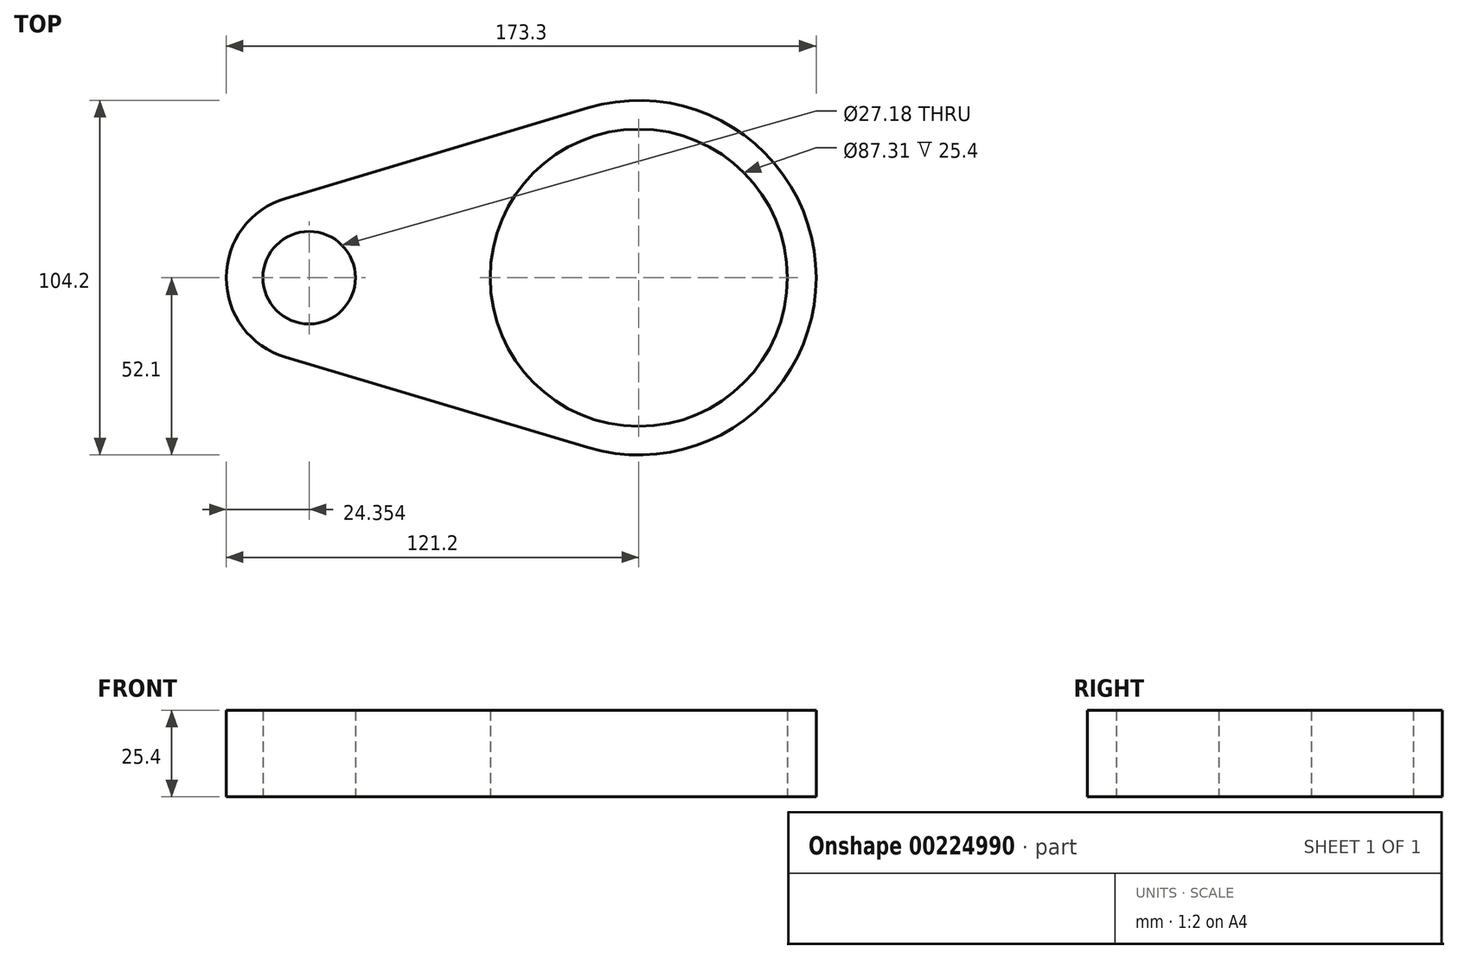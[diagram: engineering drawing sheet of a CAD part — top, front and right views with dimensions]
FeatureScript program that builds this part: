
annotation { "Feature Type Name" : "Feature", "Feature Type Description" : "" }
export const myFeature = defineFeature(function(context is Context, id is Id, definition is map)
    precondition{}
    {
        {
            var Q0;
            Q0=qCreatedBy(makeId("Top.planeOp"),FACE);
            var sketch = newSketch(context, id + "F0", { "sketchPlane" : qUnion([Q0])});
            skArc(sketch, "E0", {"start": v(-103.82, 23.33) * mm, "mid": v(-121.2, 0) * mm, "end": v(-103.82, -23.33) * mm});
            skArc(sketch, "E1", {"start": v(-14.92, -49.91) * mm, "mid": v(52.1, 0) * mm, "end": v(-14.92, 49.91) * mm});
            skLineSegment(sketch, "E2", {"start": v(-103.82, 23.33) * mm, "end": v(-14.92, 49.91) * mm});
            skLineSegment(sketch, "E3", {"start": v(-14.92, -49.91) * mm, "end": v(-103.82, -23.33) * mm});
            skCircle(sketch, "E4", {"center": v(-96.85, 0) * mm, "radius": 13.6 * mm});
            skCircle(sketch, "E5", {"center": v(0, 0) * mm, "radius": 43.66 * mm});
            skCircle(sketch, "E6", {"center": v(0, 0) * mm, "radius": 52.1 * mm});
            skSolve(sketch);
        }
        {
            var Q0;
            Q0=makeQuery(id+"F0.imprint","IMPRINT",FACE,{"disambiguationData":[TD([[makeQuery(id+"F0.imprint","IMPRINT",EDGE,{"derivedFrom":sQuery(id+"F0.wireOp",EDGE,"E0")}),1.0]])]});
            var Q1;
            Q1=makeQuery(id+"F0.imprint","IMPRINT",FACE,{"disambiguationData":[TD([[makeQuery(id+"F0.imprint","IMPRINT",EDGE,{"derivedFrom":sQuery(id+"F0.wireOp",EDGE,"E5")}),-1.0]])]});
            extrude(context, id + "F1", {"entities" : qUnion([Q0, Q1]), "depth" : 25.4 * mm});
        }
    });
